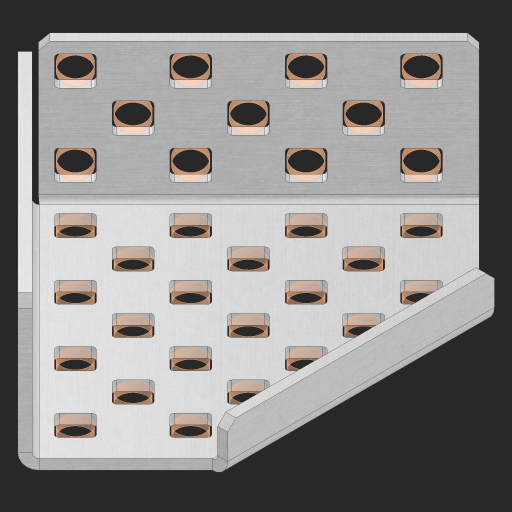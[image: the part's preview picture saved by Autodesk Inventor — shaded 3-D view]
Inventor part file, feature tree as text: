
AUTODESK INVENTOR PART (.ipt)
format: ipt  version: 2023 (Build 270158000, 158)  size: 881,664 bytes
history: native  units: in
note: dims shown in document units (in); Inventor stores cm internally (conversion verified against a paired STEP export)
features: other x44, extrude x43, pattern_linear x9, sketch x9, chamfer x1, imported_body x1
ambient origin geometry x8: Origin, YZ Plane, XZ Plane, XY Plane, X Axis, Y Axis, Z Axis, Center Point
bodies: Body1 (feature_tree), Body2 (feature_tree), Body3 (feature_tree), Body4 (feature_tree), Body5 (feature_tree), Body6 (feature_tree), Body7 (feature_tree), Body8 (feature_tree), Body9 (feature_tree), Body10 (feature_tree), Body11 (feature_tree), Body12 (feature_tree), Body13 (feature_tree), Body14 (feature_tree), Body15 (feature_tree), Body16 (feature_tree), Body17 (feature_tree), Body18 (feature_tree), Body19 (feature_tree), Body20 (feature_tree), Body21 (feature_tree), Body22 (feature_tree), Body23 (feature_tree), Body24 (feature_tree), Body25 (feature_tree), Body26 (feature_tree), Body27 (feature_tree), Body28 (feature_tree), Body29 (feature_tree), Body30 (feature_tree), Body31 (feature_tree), Body32 (feature_tree), Body33 (feature_tree), Body34 (feature_tree), Body35 (feature_tree), Body36 (feature_tree), Body37 (feature_tree), Body38 (feature_tree), Body39 (feature_tree), Body40 (feature_tree), Body41 (feature_tree), Body42 (feature_tree), Body43 (feature_tree), Body44 (feature_tree)
feature tree (107):
  other  "Angle Corner Gusset"
  chamfer  "Chamfer1"  Distance=0.062in
  pattern_linear  "Rectangular Pattern1"  Count1=4 Spacing1=0.5in
  pattern_linear  "Rectangular Pattern2"  Count1=2 Spacing1=0.5in
  pattern_linear  "Rectangular Pattern3"  Count1=3 Spacing1=0.5in
  pattern_linear  "Rectangular Pattern4"  Count1=4 Spacing1=0.5in
  pattern_linear  "Rectangular Pattern5"  Count1=2 Spacing1=0.5in
  pattern_linear  "Rectangular Pattern6"  Count1=3 Spacing1=0.5in
  pattern_linear  "Rectangular Pattern7"  Count1=2 Spacing1=0.5in
  pattern_linear  "Rectangular Pattern8"  Count1=4 Spacing1=0.5in
  pattern_linear  "Rectangular Pattern9"  Count1=3 Spacing1=0.5in
  imported_body  "Base1"
  sketch  "Sketch1"  dims[d10=0.062in d11=0.0in d12=1.1811in d14=0.5in]
  other  "Srf1"
  other  "Srf2"
  other  "Srf3"
  other  "Srf4"
  other  "Srf5"
  other  "Srf6"
  other  "Srf7"
  other  "Srf8"
  sketch  "Sketch2"  dims[d16=0.062in d17=0.0in d18=1.5748in d20=0.5in d21=0.7874in d23=0.5in]
  other  "Srf9"
  other  "Srf10"
  other  "Srf11"
  sketch  "Sketch3"  dims[d25=0.062in d26=0.0in d27=1.1811in d29=0.5in]
  other  "Srf12"
  other  "Srf13"
  other  "Srf14"
  other  "Srf15"
  other  "Srf16"
  other  "Srf17"
  other  "Srf18"
  other  "Srf19"
  sketch  "Sketch4"  dims[d31=0.062in d32=0.0in d33=0.7874in d35=0.5in d36=1.5748in d38=0.5in]
  other  "Srf20"
  other  "Srf21"
  other  "Srf22"
  sketch  "Sketch5"  dims[d40=0.062in d41=0.0in d42=1.1811in d44=0.5in]
  other  "Srf23"
  other  "Srf24"
  other  "Srf25"
  other  "Srf26"
  other  "Srf27"
  other  "Srf28"
  other  "Srf29"
  other  "Srf30"
  sketch  "Sketch6"  dims[d46=0.062in d47=0.0in d48=0.7874in d50=0.5in]
  other  "Srf31"
  other  "Srf32"
  other  "Srf33"
  sketch  "Sketch7"  dims[d52=0.062in d53=0.0in d54=0.7874in d56=0.5in]
  other  "Srf34"
  other  "Srf35"
  sketch  "Sketch8"  dims[d57=1.1811in d59=0.5in d61=0.062in d62=0.0in]
  other  "Srf36"
  other  "Srf37"
  other  "Srf38"
  other  "Srf39"
  other  "Srf40"
  other  "Srf41"
  sketch  "Sketch9"  dims[d63=0.7874in d65=0.5in]
  other  "Srf42"
  other  "Srf43"
  extrude  "ExtrusionSrf1"  Depth=0.062in
  extrude  "ExtrusionSrf9"  Depth=0.062in
  extrude  "ExtrusionSrf12"  Depth=0.062in TaperAngle=0.0deg
  extrude  "ExtrusionSrf20"  [1 undecoded]
  extrude  "ExtrusionSrf23"  [1 undecoded]
  extrude  "ExtrusionSrf31"  [1 undecoded]
  extrude  "ExtrusionSrf34"  [1 undecoded]
  extrude  "ExtrusionSrf36"  [1 undecoded]
  extrude  "ExtrusionSrf42"  [1 undecoded]
  extrude  "ExtrusionSrf2"  [1 undecoded]
  extrude  "ExtrusionSrf3"  [1 undecoded]
  extrude  "ExtrusionSrf4"  [1 undecoded]
  extrude  "ExtrusionSrf5"  [1 undecoded]
  extrude  "ExtrusionSrf6"  [1 undecoded]
  extrude  "ExtrusionSrf7"  [1 undecoded]
  extrude  "ExtrusionSrf8"  [1 undecoded]
  extrude  "ExtrusionSrf10"  [1 undecoded]
  extrude  "ExtrusionSrf11"  [1 undecoded]
  extrude  "ExtrusionSrf13"  [1 undecoded]
  extrude  "ExtrusionSrf14"  [1 undecoded]
  extrude  "ExtrusionSrf15"  [1 undecoded]
  extrude  "ExtrusionSrf16"  [1 undecoded]
  extrude  "ExtrusionSrf17"  [1 undecoded]
  extrude  "ExtrusionSrf18"  [1 undecoded]
  extrude  "ExtrusionSrf19"  [1 undecoded]
  extrude  "ExtrusionSrf21"  [1 undecoded]
  extrude  "ExtrusionSrf22"  [1 undecoded]
  extrude  "ExtrusionSrf24"  [1 undecoded]
  extrude  "ExtrusionSrf25"  [1 undecoded]
  extrude  "ExtrusionSrf26"  [1 undecoded]
  extrude  "ExtrusionSrf27"  [1 undecoded]
  extrude  "ExtrusionSrf28"  [1 undecoded]
  extrude  "ExtrusionSrf29"  [1 undecoded]
  extrude  "ExtrusionSrf30"  [1 undecoded]
  extrude  "ExtrusionSrf32"  [1 undecoded]
  extrude  "ExtrusionSrf33"  [1 undecoded]
  extrude  "ExtrusionSrf35"  [1 undecoded]
  extrude  "ExtrusionSrf37"  [1 undecoded]
  extrude  "ExtrusionSrf38"  [1 undecoded]
  extrude  "ExtrusionSrf39"  [1 undecoded]
  extrude  "ExtrusionSrf40"  [1 undecoded]
  extrude  "ExtrusionSrf41"  [1 undecoded]
  extrude  "ExtrusionSrf43"  [1 undecoded]
note: 40 required parameter values undecoded (feature->parameter linkage not recoverable at this tier; creation-order binding heuristic only, values carry confidence <= 0.55)
